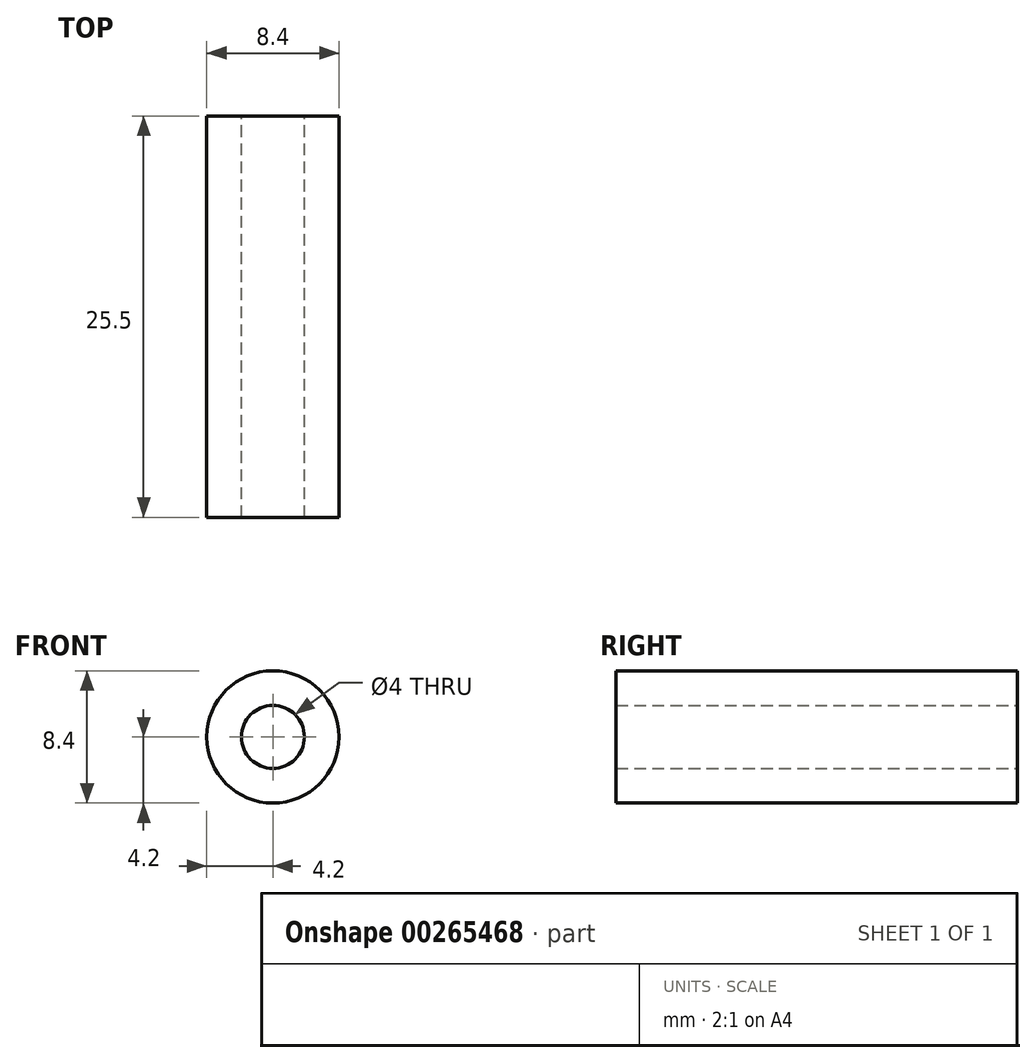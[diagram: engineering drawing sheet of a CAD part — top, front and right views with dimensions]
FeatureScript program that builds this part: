
annotation { "Feature Type Name" : "Feature", "Feature Type Description" : "" }
export const myFeature = defineFeature(function(context is Context, id is Id, definition is map)
    precondition{}
    {
        {
            var Q0;
            Q0=qCreatedBy(makeId("Front.planeOp"),FACE);
            var sketch = newSketch(context, id + "F0", { "sketchPlane" : qUnion([Q0])});
            skCircle(sketch, "E0", {"center": v(0, 0) * mm, "radius": 2 * mm});
            skCircle(sketch, "E1", {"center": v(0, 0) * mm, "radius": 4.2 * mm});
            skSolve(sketch);
        }
        {
            var Q0;
            Q0=makeQuery(id+"F0.imprint","IMPRINT",FACE,{"disambiguationData":[TD([[makeQuery(id+"F0.imprint","IMPRINT",EDGE,{"derivedFrom":sQuery(id+"F0.wireOp",EDGE,"E0")}),-1.0]])]});
            extrude(context, id + "F1", {"entities" : qUnion([Q0]), "depth" : 25.5 * mm});
        }
    });
